# Revit family: Lighting-CommercialSector-GEWISS-ELIA-PL-BACKLIT_M1-LED_FLUSH_MOUNTING
name_source: partatom
category: Apparecchi per illuminazione
units: mm (PartAtom-declared; Revit-internal decimal feet)

## family parameters
Condiviso = No
Host = Superficie
Punto di calcolo locali = Sì
Quota connettore circolare = Usa diametro
Sorgente d'illuminazione = Sì
Taglio con vuoti quando caricato = No
Tipo di parte = Normale

## types (4) — shared parameters
- = -
-- = -
--- = -
---- = -
----- = -
Angolo inclinazione = 60.00°
Application = Internal
Category: = Floor lighting
Classification: = -
Color Rendering Index = CRI 80
Colour = White
Colour : = Powder coating
DIN 18032-3 certification = -
Device with reduced surface temperature = -
Driver Box = -
Efficiency (lm/W): = Above 110 lm/W
Electrocod = 2419
Eletrical and lighting features = -
Emetti da larghezza rettangolo = 300 mm  [stored 0.984252 ft]
Emetti da lunghezza rettangolo = 1200 mm
External screw = -
FORO_CONTROSOFFITTO = 47 mm
File diagramma fotometrico = generic
Filtro dei colori = 16777215
Gasket = -
General information = -
Glow Wire Test : = 650 °C
Group: = xyz
IDF = 6cc619cf-8d41-4609-9561-c7dab0f6a82f
IP degree = IP40
IPEA = -
Immagine tipo = <Nessuno>
Installationa and maintenance = -
Insulation class = II
LED = led
LED Maintenance = By professional
Larghezza_Lampada = 300 mm  [stored 0.984252 ft]
Lifetime = L80B50 (Tq25°) = 50.000h
Locking Hook = -
Lunghezza_lampada = 1200 mm
Materials = -
Maximum surface exposed to the wind : = -
Operating temperature : = -20° +45°
Optic = Wide opal
Optic Maintenance = Non-replaceable
Optic and illuminating features = -
POSIZIONE = 80000
Photobiological Risk Class = RG0
Produttore = GEWISS S.p.A.
Prospetto di default = 1219 mm
Rated frequency (Hz) = 50/60 Hz
Rendi la forma visibile nel rendering = No
SEO = Luminaire
STRUTTURA = <Per categoria>
Shock resistance = IK03
Spessore lampada = 27 mm
Standard Deviation Colour Matching = SDCM = 3
Standards and approvals = -
Stocking temperature = -20° +65°
Supply voltage = 220-240 VÂ
System  power = From 20 to 30 W
Tilt- = With suspension adjustment Kit
Type of light source = LED
Typology: = xyz
URL = https://www.gewiss.com
Unique digital code (Datamatrix) = Currently not present
Variazione temperatura colore lampada con luminosità attenuata = <Nessuno>
Version file RFA = 20.0
Warranty = 5 years
Wiring = With connection terminal on driver

## per-type parameters (varying)
| type | Control System | Descrizione | Lumen output  (lm) | Modello |
| GWF1610LT830 - ELIA PL Backlit M1 300x1200mm 3000K CRI80 On/Off Opal | ON / OFF | ELIA PL Backlit M1 300x1200mm 3000K CRI80 On/Off Opal | Above 3,000 lm | GWF1610LT830 |
| GWF1611LT840 - ELIA PL Backlit M1 300x1200mm 4000K CRI80 DALI Opal | DALI | ELIA PL Backlit M1 300x1200mm 4000K CRI80 DALI Opal | Above 3,000 lm | GWF1611LT840 |
| GWF1611LT830 - ELIA PL Backlit M1 300x1200mm 3000K CRI80 DALI Opal | DALI | ELIA PL Backlit M1 300x1200mm 3000K CRI80 DALI Opal | From 2,000 to 3,000 lm | GWF1611LT830 |
| GWF1610LT840 - ELIA PL Backlit M1 300x1200mm 4000K CRI80 On/Off Opal | ON / OFF | ELIA PL Backlit M1 300x1200mm 4000K CRI80 On/Off Opal | Above 3,000 lm | GWF1610LT840 |

note: [stored X ft] marks values corroborated as IEEE doubles in the binary element streams (Revit-internal decimal feet)

## geometry (parser evidence)
native form markers: Sweep x3
no freeform markers — native parametric forms only
